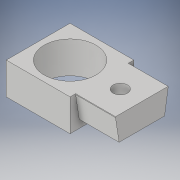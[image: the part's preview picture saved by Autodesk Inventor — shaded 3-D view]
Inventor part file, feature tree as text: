
AUTODESK INVENTOR PART (.ipt)
format: ipt  version: 2018 (Build 220112000, 112)  size: 140,288 bytes
history: native  units: in
note: dims shown in document units (in); Inventor stores cm internally (conversion verified against a paired STEP export)
features: extrude x5, sketch x5, projected_geometry x1
ambient origin geometry x8: Origin, YZ Plane, XZ Plane, XY Plane, X Axis, Y Axis, Z Axis, Center Point
bodies: Solid1 (feature_tree)
feature tree (11):
  extrude  "Extrusion1"  Depth=0.8in
  extrude  "Extrusion2"  Depth=0.4in
  extrude  "Extrusion3"  Depth=0.5in TaperAngle=0.0deg
  extrude  "Extrusion4"  Depth=0.66in
  extrude  "Extrusion5"  Depth=0.1in
  sketch  "Sketch1"  dims[d0=0.8in d1=0.8in]
  sketch  "Sketch2"  dims[d2=0.4in d3=0.4in]
  sketch  "Sketch3"  dims[d4=0.65in d5=0.5in d6=0.0in]
  sketch  "Sketch4"  dims[d7=0.66in d8=0.57in]
  projected_geometry  "Projected Loop1"
  sketch  "Sketch5"  dims[d9=0.29in d10=0.2in d11=0.115in d12=0.5in d13=0.0in d14=0.18in d15=0.27in d16=0.7in d17=0.0in d18=1.0in d19=0.0in d20=0.1in d21=0.0in]
